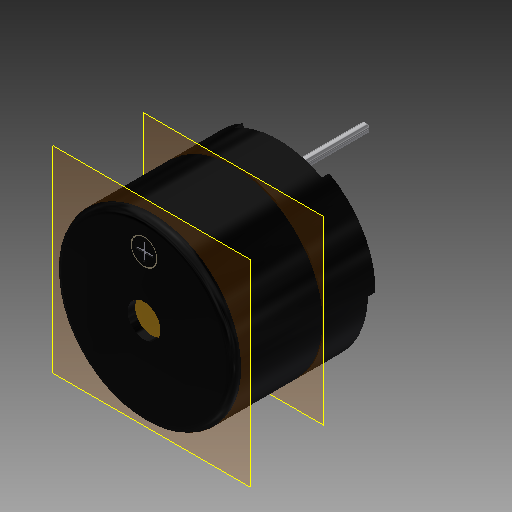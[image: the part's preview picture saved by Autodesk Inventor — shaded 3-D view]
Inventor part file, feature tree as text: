
AUTODESK INVENTOR PART (.ipt)
format: ipt  version: 2019 (Build 230136000, 136)  size: 224,768 bytes
history: native  units: mm
features: extrude x10, sketch x10, plane x2, fillet x1, pattern_circular x1, chamfer x1, projected_geometry x1
ambient origin geometry x8: Origin, YZ Plane, XZ Plane, XY Plane, X Axis, Y Axis, Z Axis, Center Point
bodies: Solid1 (feature_tree)
feature tree (26):
  extrude  "Extrusion1"  Depth=9.5mm TaperAngle=0.0deg
  plane  "Work Plane1"
  extrude  "Extrusion2"  Depth=8.5mm
  extrude  "Extrusion3"  Depth=1.0mm
  extrude  "Extrusion4"  Depth=0.5mm
  fillet  "Fillet1"  Radius=0.5mm
  extrude  "Extrusion5"  Depth=0.5mm TaperAngle=0.0deg
  pattern_circular  "Circular Pattern1"  Count=3 Angle=360.0deg
  extrude  "Extrusion6"  Depth=3.8mm
  extrude  "Extrusion7"  Depth=6.0mm
  chamfer  "Chamfer1"  Distance=4.0mm
  extrude  "Extrusion8"  Depth=0.1mm TaperAngle=0.0deg
  extrude  "Extrusion9"  [1 undecoded]
  plane  "Work Plane2"
  extrude  "Extrusion10"  Depth=11.5mm
  sketch  "Sketch1"  dims[d0=12.0mm d1=9.5mm d2=0.0mm]
  sketch  "Sketch2"  dims[d3=-0.5mm d4=8.5mm]
  projected_geometry  "Projected Loop1"
  sketch  "Sketch3"  dims[d5=1.0mm d6=0.0mm d7=2.2mm]
  sketch  "Sketch4"  dims[d8=0.5mm d9=0.0mm d10=10.5mm d11=0.5mm d12=0.0mm]
  sketch  "Sketch5"  dims[d13=0.5mm d14=0.5mm d15=0.0mm d16=30.0mm d17=360.0deg]
  sketch  "Sketch6"  dims[d19=0.6mm d20=3.8mm]
  sketch  "Sketch7"  dims[d21=6.0mm d22=0.0mm d23=0.6mm]
  sketch  "Sketch8"  dims[d24=3.8mm d25=4.0mm d26=0.0mm]
  sketch  "Sketch9"  dims[d27=0.2mm d28=2.0mm d29=45.0deg d30=0.1mm d31=0.0mm]
  sketch  "Sketch10"  dims[d32=0.01mm d33=0.0mm d34=-6.0mm d35=11.5mm d36=0.1mm d37=0.0mm]
note: 1 required parameter value undecoded (feature->parameter linkage not recoverable at this tier; creation-order binding heuristic only, values carry confidence <= 0.55)
